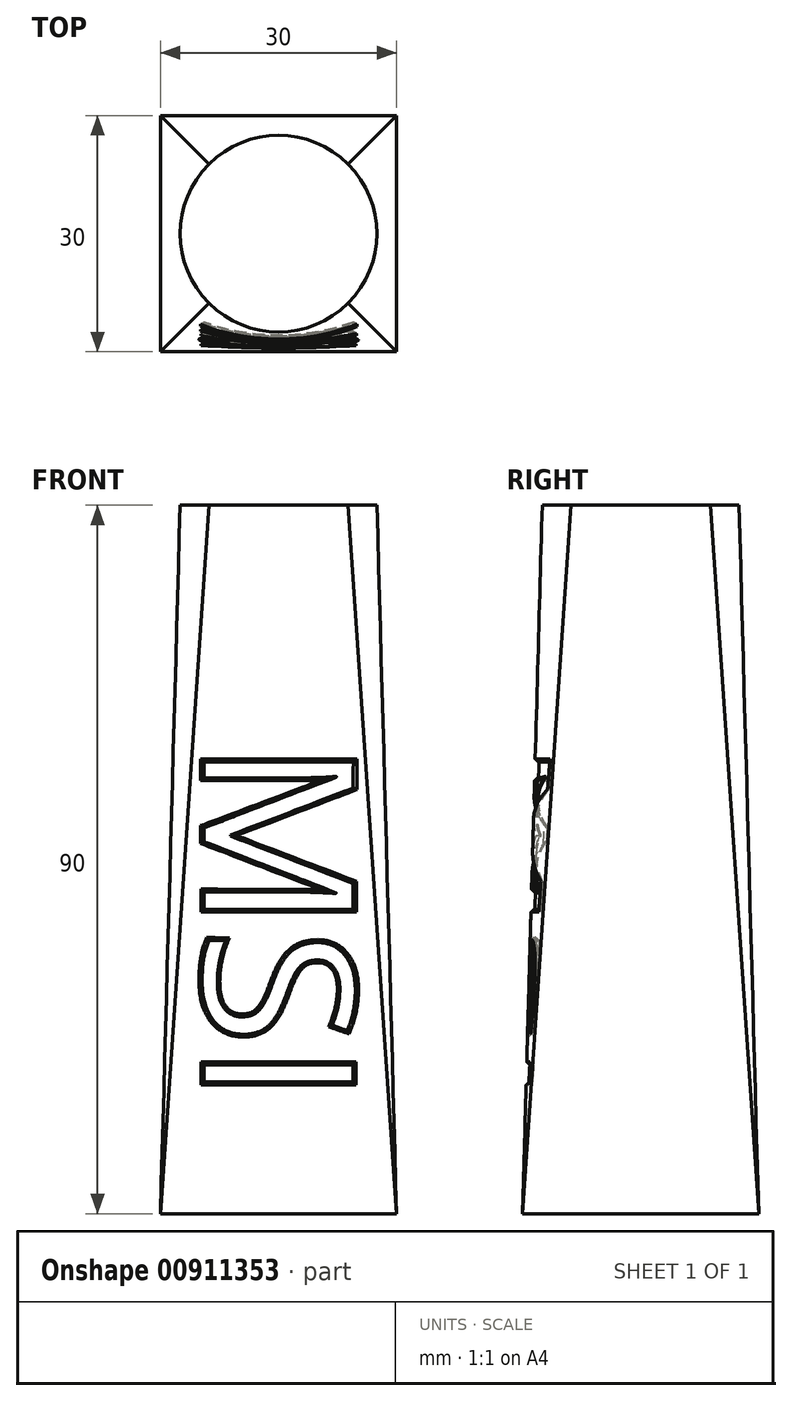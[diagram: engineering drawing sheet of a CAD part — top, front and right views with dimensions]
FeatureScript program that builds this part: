
annotation { "Feature Type Name" : "Feature", "Feature Type Description" : "" }
export const myFeature = defineFeature(function(context is Context, id is Id, definition is map)
    precondition{}
    {
        {
            var Q0;
            Q0=qCreatedBy(makeId("Top.planeOp"),FACE);
            var sketch = newSketch(context, id + "F0", { "sketchPlane" : qUnion([Q0])});
            skLineSegment(sketch, "E0.bottom", {"start": v(15, -15) * mm, "end": v(-15, -15) * mm});
            skLineSegment(sketch, "E0.top", {"start": v(15, 15) * mm, "end": v(-15, 15) * mm});
            skLineSegment(sketch, "E0.left", {"start": v(15, -15) * mm, "end": v(15, 15) * mm});
            skLineSegment(sketch, "E0.right", {"start": v(-15, -15) * mm, "end": v(-15, 15) * mm});
            skPoint(sketch, "E0.middle", {"position": v(0, 0) * mm});
            skSolve(sketch);
        }
        {
            var Q0;
            Q0=qCreatedBy(makeId("Top.planeOp"),FACE);
            cPlane(context, id + "F1", {"entities" : qUnion([Q0]), "cplaneType" : CPlaneType.OFFSET, "offset" : 90 * mm, "width" : 150 * mm, "height" : 150 * mm});
        }
        {
            var Q0;
            Q0=qCreatedBy(id+"F1.planeOp",FACE);
            var sketch = newSketch(context, id + "F2", { "sketchPlane" : qUnion([Q0])});
            skCircle(sketch, "E1", {"center": v(0, 0) * mm, "radius": 12.5 * mm});
            skSolve(sketch);
        }
        {
            var Q0;
            Q0=makeQuery(id+"F2.imprint","IMPRINT",FACE,{"disambiguationData":[TD([[makeQuery(id+"F2.imprint","IMPRINT",EDGE,{"derivedFrom":sQuery(id+"F2.wireOp",EDGE,"E1")}),1.0]])]});
            var Q1;
            Q1=makeQuery(id+"F0.imprint","IMPRINT",FACE,{"disambiguationData":[TD([[makeQuery(id+"F0.imprint","IMPRINT",EDGE,{"derivedFrom":sQuery(id+"F0.wireOp",EDGE,"E0.bottom")}),-1.0]])]});
            loft(context, id + "F3", {"sheetProfilesArray" : [{ "sheetProfileEntities" : qUnion([Q0]) }, { "sheetProfileEntities" : qUnion([Q1]) }]});
        }
        {
            var Q0;
            Q0=qCreatedBy(makeId("Front.planeOp"),FACE);
            cPlane(context, id + "F4", {"entities" : qUnion([Q0]), "cplaneType" : CPlaneType.OFFSET, "offset" : 75 * mm, "width" : 150 * mm, "height" : 150 * mm});
        }
        {
            var Q0;
            Q0=qCreatedBy(id+"F4.planeOp",FACE);
            var sketch = newSketch(context, id + "F5", { "sketchPlane" : qUnion([Q0])});
            skText(sketch, "E2", { "text": "MSI", "fontName": "OpenSans-Regular.ttf"});
            const initialGuessF5  = {"E2": [-0.00944, 0.06, 0, -1, 0.01909]};
            skSetInitialGuess(sketch, initialGuessF5);
            skSolve(sketch);
        }
        {
            var Q0;
            Q0=qSketchRegion(id+"F5",true);
            var Q1;
            Q1=makeQuery(id+"F3.opLoft","SWEPT_BODY",BODY,{"disambiguationData":[OSD([makeQuery(id+"F0.imprint","IMPRINT",FACE,{"disambiguationData":[TD([[makeQuery(id+"F0.imprint","IMPRINT",EDGE,{"derivedFrom":sQuery(id+"F0.wireOp",EDGE,"E0.bottom")}),-1.0]])]}),makeQuery(id+"F2.imprint","IMPRINT",FACE,{"disambiguationData":[TD([[makeQuery(id+"F2.imprint","IMPRINT",EDGE,{"derivedFrom":sQuery(id+"F2.wireOp",EDGE,"E1")}),1.0]])]})])]});
            extrude(context, id + "F6", {"entities" : qUnion([Q0]), "operationType" : NewBodyOperationType.REMOVE, "endBound" : BoundingType.UP_TO_BODY, "oppositeDirection" : true, "depth" : 25 * mm, "endBoundEntityBody" : qUnion([Q1]), "hasOffset" : true, "offsetDistance" : .5 * mm, "offsetOppositeDirection" : true});
        }
        {
            var Q0;
            Q0=makeQuery(id+"F6.boolean.opBoolean","INTERSECT",EDGE,{"derivedFrom":[makeQuery(id+"F3.opLoft","SWEPT_FACE",FACE,{"disambiguationData":[OSD([sQuery(id+"F0.wireOp",EDGE,"E0.bottom"),sQuery(id+"F0.wireOp",EDGE,"E0.left"),sQuery(id+"F0.wireOp",EDGE,"E0.right"),sQuery(id+"F2.wireOp",EDGE,"E1")])]}),makeQuery(id+"F6.opExtrude","SWEPT_FACE",FACE,{"disambiguationData":[OSD([sQuery(id+"F5.wireOp",EDGE,"E2.sketch_text.stroke-0")])]})]});
            var Q1;
            Q1=makeQuery(id+"F6.boolean.opBoolean","INTERSECT",EDGE,{"derivedFrom":[makeQuery(id+"F3.opLoft","SWEPT_FACE",FACE,{"disambiguationData":[OSD([sQuery(id+"F0.wireOp",EDGE,"E0.bottom"),sQuery(id+"F0.wireOp",EDGE,"E0.left"),sQuery(id+"F0.wireOp",EDGE,"E0.right"),sQuery(id+"F2.wireOp",EDGE,"E1")])]}),makeQuery(id+"F6.opExtrude","SWEPT_FACE",FACE,{"disambiguationData":[OSD([sQuery(id+"F5.wireOp",EDGE,"E2.sketch_text.stroke-7")])]})]});
            var Q2;
            Q2=makeQuery(id+"F6.boolean.opBoolean","INTERSECT",EDGE,{"derivedFrom":[makeQuery(id+"F3.opLoft","SWEPT_FACE",FACE,{"disambiguationData":[OSD([sQuery(id+"F0.wireOp",EDGE,"E0.bottom"),sQuery(id+"F0.wireOp",EDGE,"E0.left"),sQuery(id+"F0.wireOp",EDGE,"E0.right"),sQuery(id+"F2.wireOp",EDGE,"E1")])]}),makeQuery(id+"F6.opExtrude","SWEPT_FACE",FACE,{"disambiguationData":[OSD([sQuery(id+"F5.wireOp",EDGE,"E2.sketch_text.stroke-9")])]})]});
            var Q3;
            Q3=makeQuery(id+"F6.boolean.opBoolean","INTERSECT",EDGE,{"derivedFrom":[makeQuery(id+"F3.opLoft","SWEPT_FACE",FACE,{"disambiguationData":[OSD([sQuery(id+"F0.wireOp",EDGE,"E0.bottom"),sQuery(id+"F0.wireOp",EDGE,"E0.left"),sQuery(id+"F0.wireOp",EDGE,"E0.right"),sQuery(id+"F2.wireOp",EDGE,"E1")])]}),makeQuery(id+"F6.opExtrude","SWEPT_FACE",FACE,{"disambiguationData":[OSD([sQuery(id+"F5.wireOp",EDGE,"E2.sketch_text.stroke-5")])]})]});
            var Q4;
            Q4=makeQuery(id+"F6.boolean.opBoolean","INTERSECT",EDGE,{"derivedFrom":[makeQuery(id+"F3.opLoft","SWEPT_FACE",FACE,{"disambiguationData":[OSD([sQuery(id+"F0.wireOp",EDGE,"E0.bottom"),sQuery(id+"F0.wireOp",EDGE,"E0.left"),sQuery(id+"F0.wireOp",EDGE,"E0.right"),sQuery(id+"F2.wireOp",EDGE,"E1")])]}),makeQuery(id+"F6.opExtrude","SWEPT_FACE",FACE,{"disambiguationData":[OSD([sQuery(id+"F5.wireOp",EDGE,"E2.sketch_text.stroke-6")])]})]});
            var Q5;
            Q5=makeQuery(id+"F6.boolean.opBoolean","INTERSECT",EDGE,{"derivedFrom":[makeQuery(id+"F3.opLoft","SWEPT_FACE",FACE,{"disambiguationData":[OSD([sQuery(id+"F0.wireOp",EDGE,"E0.bottom"),sQuery(id+"F0.wireOp",EDGE,"E0.left"),sQuery(id+"F0.wireOp",EDGE,"E0.right"),sQuery(id+"F2.wireOp",EDGE,"E1")])]}),makeQuery(id+"F6.opExtrude","SWEPT_FACE",FACE,{"disambiguationData":[OSD([sQuery(id+"F5.wireOp",EDGE,"E2.sketch_text.stroke-4")])]})]});
            var Q6;
            Q6=makeQuery(id+"F6.boolean.opBoolean","INTERSECT",EDGE,{"derivedFrom":[makeQuery(id+"F3.opLoft","SWEPT_FACE",FACE,{"disambiguationData":[OSD([sQuery(id+"F0.wireOp",EDGE,"E0.bottom"),sQuery(id+"F0.wireOp",EDGE,"E0.left"),sQuery(id+"F0.wireOp",EDGE,"E0.right"),sQuery(id+"F2.wireOp",EDGE,"E1")])]}),makeQuery(id+"F6.opExtrude","SWEPT_FACE",FACE,{"disambiguationData":[OSD([sQuery(id+"F5.wireOp",EDGE,"E2.sketch_text.stroke-3")])]})]});
            var Q7;
            Q7=makeQuery(id+"F6.boolean.opBoolean","INTERSECT",EDGE,{"derivedFrom":[makeQuery(id+"F3.opLoft","SWEPT_FACE",FACE,{"disambiguationData":[OSD([sQuery(id+"F0.wireOp",EDGE,"E0.bottom"),sQuery(id+"F0.wireOp",EDGE,"E0.left"),sQuery(id+"F0.wireOp",EDGE,"E0.right"),sQuery(id+"F2.wireOp",EDGE,"E1")])]}),makeQuery(id+"F6.opExtrude","SWEPT_FACE",FACE,{"disambiguationData":[OSD([sQuery(id+"F5.wireOp",EDGE,"E2.sketch_text.stroke-2")])]})]});
            var Q8;
            Q8=makeQuery(id+"F6.boolean.opBoolean","INTERSECT",EDGE,{"derivedFrom":[makeQuery(id+"F3.opLoft","SWEPT_FACE",FACE,{"disambiguationData":[OSD([sQuery(id+"F0.wireOp",EDGE,"E0.bottom"),sQuery(id+"F0.wireOp",EDGE,"E0.left"),sQuery(id+"F0.wireOp",EDGE,"E0.right"),sQuery(id+"F2.wireOp",EDGE,"E1")])]}),makeQuery(id+"F6.opExtrude","SWEPT_FACE",FACE,{"disambiguationData":[OSD([sQuery(id+"F5.wireOp",EDGE,"E2.sketch_text.stroke-17")])]})]});
            var Q9;
            Q9=makeQuery(id+"F6.boolean.opBoolean","INTERSECT",EDGE,{"derivedFrom":[makeQuery(id+"F3.opLoft","SWEPT_FACE",FACE,{"disambiguationData":[OSD([sQuery(id+"F0.wireOp",EDGE,"E0.bottom"),sQuery(id+"F0.wireOp",EDGE,"E0.left"),sQuery(id+"F0.wireOp",EDGE,"E0.right"),sQuery(id+"F2.wireOp",EDGE,"E1")])]}),makeQuery(id+"F6.opExtrude","SWEPT_FACE",FACE,{"disambiguationData":[OSD([sQuery(id+"F5.wireOp",EDGE,"E2.sketch_text.stroke-16")])]})]});
            var Q10;
            Q10=makeQuery(id+"F6.boolean.opBoolean","INTERSECT",EDGE,{"derivedFrom":[makeQuery(id+"F3.opLoft","SWEPT_FACE",FACE,{"disambiguationData":[OSD([sQuery(id+"F0.wireOp",EDGE,"E0.bottom"),sQuery(id+"F0.wireOp",EDGE,"E0.left"),sQuery(id+"F0.wireOp",EDGE,"E0.right"),sQuery(id+"F2.wireOp",EDGE,"E1")])]}),makeQuery(id+"F6.opExtrude","SWEPT_FACE",FACE,{"disambiguationData":[OSD([sQuery(id+"F5.wireOp",EDGE,"E2.sketch_text.stroke-14")])]})]});
            var Q11;
            Q11=makeQuery(id+"F6.boolean.opBoolean","INTERSECT",EDGE,{"derivedFrom":[makeQuery(id+"F3.opLoft","SWEPT_FACE",FACE,{"disambiguationData":[OSD([sQuery(id+"F0.wireOp",EDGE,"E0.bottom"),sQuery(id+"F0.wireOp",EDGE,"E0.left"),sQuery(id+"F0.wireOp",EDGE,"E0.right"),sQuery(id+"F2.wireOp",EDGE,"E1")])]}),makeQuery(id+"F6.opExtrude","SWEPT_FACE",FACE,{"disambiguationData":[OSD([sQuery(id+"F5.wireOp",EDGE,"E2.sketch_text.stroke-13")])]})]});
            var Q12;
            Q12=makeQuery(id+"F6.boolean.opBoolean","INTERSECT",EDGE,{"derivedFrom":[makeQuery(id+"F3.opLoft","SWEPT_FACE",FACE,{"disambiguationData":[OSD([sQuery(id+"F0.wireOp",EDGE,"E0.bottom"),sQuery(id+"F0.wireOp",EDGE,"E0.left"),sQuery(id+"F0.wireOp",EDGE,"E0.right"),sQuery(id+"F2.wireOp",EDGE,"E1")])]}),makeQuery(id+"F6.opExtrude","SWEPT_FACE",FACE,{"disambiguationData":[OSD([sQuery(id+"F5.wireOp",EDGE,"E2.sketch_text.stroke-12")])]})]});
            var Q13;
            Q13=makeQuery(id+"F6.boolean.opBoolean","INTERSECT",EDGE,{"derivedFrom":[makeQuery(id+"F3.opLoft","SWEPT_FACE",FACE,{"disambiguationData":[OSD([sQuery(id+"F0.wireOp",EDGE,"E0.bottom"),sQuery(id+"F0.wireOp",EDGE,"E0.left"),sQuery(id+"F0.wireOp",EDGE,"E0.right"),sQuery(id+"F2.wireOp",EDGE,"E1")])]}),makeQuery(id+"F6.opExtrude","SWEPT_FACE",FACE,{"disambiguationData":[OSD([sQuery(id+"F5.wireOp",EDGE,"E2.sketch_text.stroke-11")])]})]});
            var Q14;
            Q14=makeQuery(id+"F6.boolean.opBoolean","INTERSECT",EDGE,{"derivedFrom":[makeQuery(id+"F3.opLoft","SWEPT_FACE",FACE,{"disambiguationData":[OSD([sQuery(id+"F0.wireOp",EDGE,"E0.bottom"),sQuery(id+"F0.wireOp",EDGE,"E0.left"),sQuery(id+"F0.wireOp",EDGE,"E0.right"),sQuery(id+"F2.wireOp",EDGE,"E1")])]}),makeQuery(id+"F6.opExtrude","SWEPT_FACE",FACE,{"disambiguationData":[OSD([sQuery(id+"F5.wireOp",EDGE,"E2.sketch_text.stroke-10")])]})]});
            var Q15;
            Q15=makeQuery(id+"F6.boolean.opBoolean","INTERSECT",EDGE,{"derivedFrom":[makeQuery(id+"F3.opLoft","SWEPT_FACE",FACE,{"disambiguationData":[OSD([sQuery(id+"F0.wireOp",EDGE,"E0.bottom"),sQuery(id+"F0.wireOp",EDGE,"E0.left"),sQuery(id+"F0.wireOp",EDGE,"E0.right"),sQuery(id+"F2.wireOp",EDGE,"E1")])]}),makeQuery(id+"F6.opExtrude","SWEPT_FACE",FACE,{"disambiguationData":[OSD([sQuery(id+"F5.wireOp",EDGE,"E2.sketch_text.stroke-32")])]})]});
            var Q16;
            Q16=makeQuery(id+"F6.boolean.opBoolean","INTERSECT",EDGE,{"derivedFrom":[makeQuery(id+"F3.opLoft","SWEPT_FACE",FACE,{"disambiguationData":[OSD([sQuery(id+"F0.wireOp",EDGE,"E0.bottom"),sQuery(id+"F0.wireOp",EDGE,"E0.left"),sQuery(id+"F0.wireOp",EDGE,"E0.right"),sQuery(id+"F2.wireOp",EDGE,"E1")])]}),makeQuery(id+"F6.opExtrude","SWEPT_FACE",FACE,{"disambiguationData":[OSD([sQuery(id+"F5.wireOp",EDGE,"E2.sketch_text.stroke-31")])]})]});
            var Q17;
            Q17=makeQuery(id+"F6.boolean.opBoolean","INTERSECT",EDGE,{"derivedFrom":[makeQuery(id+"F3.opLoft","SWEPT_FACE",FACE,{"disambiguationData":[OSD([sQuery(id+"F0.wireOp",EDGE,"E0.bottom"),sQuery(id+"F0.wireOp",EDGE,"E0.left"),sQuery(id+"F0.wireOp",EDGE,"E0.right"),sQuery(id+"F2.wireOp",EDGE,"E1")])]}),makeQuery(id+"F6.opExtrude","SWEPT_FACE",FACE,{"disambiguationData":[OSD([sQuery(id+"F5.wireOp",EDGE,"E2.sketch_text.stroke-30")])]})]});
            var Q18;
            Q18=makeQuery(id+"F6.boolean.opBoolean","INTERSECT",EDGE,{"derivedFrom":[makeQuery(id+"F3.opLoft","SWEPT_FACE",FACE,{"disambiguationData":[OSD([sQuery(id+"F0.wireOp",EDGE,"E0.bottom"),sQuery(id+"F0.wireOp",EDGE,"E0.left"),sQuery(id+"F0.wireOp",EDGE,"E0.right"),sQuery(id+"F2.wireOp",EDGE,"E1")])]}),makeQuery(id+"F6.opExtrude","SWEPT_FACE",FACE,{"disambiguationData":[OSD([sQuery(id+"F5.wireOp",EDGE,"E2.sketch_text.stroke-29")])]})]});
            var Q19;
            Q19=makeQuery(id+"F6.boolean.opBoolean","INTERSECT",EDGE,{"derivedFrom":[makeQuery(id+"F3.opLoft","SWEPT_FACE",FACE,{"disambiguationData":[OSD([sQuery(id+"F0.wireOp",EDGE,"E0.bottom"),sQuery(id+"F0.wireOp",EDGE,"E0.left"),sQuery(id+"F0.wireOp",EDGE,"E0.right"),sQuery(id+"F2.wireOp",EDGE,"E1")])]}),makeQuery(id+"F6.opExtrude","SWEPT_FACE",FACE,{"disambiguationData":[OSD([sQuery(id+"F5.wireOp",EDGE,"E2.sketch_text.stroke-28")])]})]});
            var Q20;
            Q20=makeQuery(id+"F6.boolean.opBoolean","INTERSECT",EDGE,{"derivedFrom":[makeQuery(id+"F3.opLoft","SWEPT_FACE",FACE,{"disambiguationData":[OSD([sQuery(id+"F0.wireOp",EDGE,"E0.bottom"),sQuery(id+"F0.wireOp",EDGE,"E0.left"),sQuery(id+"F0.wireOp",EDGE,"E0.right"),sQuery(id+"F2.wireOp",EDGE,"E1")])]}),makeQuery(id+"F6.opExtrude","SWEPT_FACE",FACE,{"disambiguationData":[OSD([sQuery(id+"F5.wireOp",EDGE,"E2.sketch_text.stroke-27")])]})]});
            var Q21;
            Q21=makeQuery(id+"F6.boolean.opBoolean","INTERSECT",EDGE,{"derivedFrom":[makeQuery(id+"F3.opLoft","SWEPT_FACE",FACE,{"disambiguationData":[OSD([sQuery(id+"F0.wireOp",EDGE,"E0.bottom"),sQuery(id+"F0.wireOp",EDGE,"E0.left"),sQuery(id+"F0.wireOp",EDGE,"E0.right"),sQuery(id+"F2.wireOp",EDGE,"E1")])]}),makeQuery(id+"F6.opExtrude","SWEPT_FACE",FACE,{"disambiguationData":[OSD([sQuery(id+"F5.wireOp",EDGE,"E2.sketch_text.stroke-26")])]})]});
            var Q22;
            Q22=makeQuery(id+"F6.boolean.opBoolean","INTERSECT",EDGE,{"derivedFrom":[makeQuery(id+"F3.opLoft","SWEPT_FACE",FACE,{"disambiguationData":[OSD([sQuery(id+"F0.wireOp",EDGE,"E0.bottom"),sQuery(id+"F0.wireOp",EDGE,"E0.left"),sQuery(id+"F0.wireOp",EDGE,"E0.right"),sQuery(id+"F2.wireOp",EDGE,"E1")])]}),makeQuery(id+"F6.opExtrude","SWEPT_FACE",FACE,{"disambiguationData":[OSD([sQuery(id+"F5.wireOp",EDGE,"E2.sketch_text.stroke-25")])]})]});
            var Q23;
            Q23=makeQuery(id+"F6.boolean.opBoolean","INTERSECT",EDGE,{"derivedFrom":[makeQuery(id+"F3.opLoft","SWEPT_FACE",FACE,{"disambiguationData":[OSD([sQuery(id+"F0.wireOp",EDGE,"E0.bottom"),sQuery(id+"F0.wireOp",EDGE,"E0.left"),sQuery(id+"F0.wireOp",EDGE,"E0.right"),sQuery(id+"F2.wireOp",EDGE,"E1")])]}),makeQuery(id+"F6.opExtrude","SWEPT_FACE",FACE,{"disambiguationData":[OSD([sQuery(id+"F5.wireOp",EDGE,"E2.sketch_text.stroke-24")])]})]});
            var Q24;
            Q24=makeQuery(id+"F6.boolean.opBoolean","INTERSECT",EDGE,{"derivedFrom":[makeQuery(id+"F3.opLoft","SWEPT_FACE",FACE,{"disambiguationData":[OSD([sQuery(id+"F0.wireOp",EDGE,"E0.bottom"),sQuery(id+"F0.wireOp",EDGE,"E0.left"),sQuery(id+"F0.wireOp",EDGE,"E0.right"),sQuery(id+"F2.wireOp",EDGE,"E1")])]}),makeQuery(id+"F6.opExtrude","SWEPT_FACE",FACE,{"disambiguationData":[OSD([sQuery(id+"F5.wireOp",EDGE,"E2.sketch_text.stroke-23")])]})]});
            var Q25;
            Q25=makeQuery(id+"F6.boolean.opBoolean","INTERSECT",EDGE,{"derivedFrom":[makeQuery(id+"F3.opLoft","SWEPT_FACE",FACE,{"disambiguationData":[OSD([sQuery(id+"F0.wireOp",EDGE,"E0.bottom"),sQuery(id+"F0.wireOp",EDGE,"E0.left"),sQuery(id+"F0.wireOp",EDGE,"E0.right"),sQuery(id+"F2.wireOp",EDGE,"E1")])]}),makeQuery(id+"F6.opExtrude","SWEPT_FACE",FACE,{"disambiguationData":[OSD([sQuery(id+"F5.wireOp",EDGE,"E2.sketch_text.stroke-22")])]})]});
            var Q26;
            Q26=makeQuery(id+"F6.boolean.opBoolean","INTERSECT",EDGE,{"derivedFrom":[makeQuery(id+"F3.opLoft","SWEPT_FACE",FACE,{"disambiguationData":[OSD([sQuery(id+"F0.wireOp",EDGE,"E0.bottom"),sQuery(id+"F0.wireOp",EDGE,"E0.left"),sQuery(id+"F0.wireOp",EDGE,"E0.right"),sQuery(id+"F2.wireOp",EDGE,"E1")])]}),makeQuery(id+"F6.opExtrude","SWEPT_FACE",FACE,{"disambiguationData":[OSD([sQuery(id+"F5.wireOp",EDGE,"E2.sketch_text.stroke-21")])]})]});
            var Q27;
            Q27=makeQuery(id+"F6.boolean.opBoolean","INTERSECT",EDGE,{"derivedFrom":[makeQuery(id+"F3.opLoft","SWEPT_FACE",FACE,{"disambiguationData":[OSD([sQuery(id+"F0.wireOp",EDGE,"E0.bottom"),sQuery(id+"F0.wireOp",EDGE,"E0.left"),sQuery(id+"F0.wireOp",EDGE,"E0.right"),sQuery(id+"F2.wireOp",EDGE,"E1")])]}),makeQuery(id+"F6.opExtrude","SWEPT_FACE",FACE,{"disambiguationData":[OSD([sQuery(id+"F5.wireOp",EDGE,"E2.sketch_text.stroke-20")])]})]});
            var Q28;
            Q28=makeQuery(id+"F6.boolean.opBoolean","INTERSECT",EDGE,{"derivedFrom":[makeQuery(id+"F3.opLoft","SWEPT_FACE",FACE,{"disambiguationData":[OSD([sQuery(id+"F0.wireOp",EDGE,"E0.bottom"),sQuery(id+"F0.wireOp",EDGE,"E0.left"),sQuery(id+"F0.wireOp",EDGE,"E0.right"),sQuery(id+"F2.wireOp",EDGE,"E1")])]}),makeQuery(id+"F6.opExtrude","SWEPT_FACE",FACE,{"disambiguationData":[OSD([sQuery(id+"F5.wireOp",EDGE,"E2.sketch_text.stroke-19")])]})]});
            var Q29;
            Q29=makeQuery(id+"F6.boolean.opBoolean","INTERSECT",EDGE,{"derivedFrom":[makeQuery(id+"F3.opLoft","SWEPT_FACE",FACE,{"disambiguationData":[OSD([sQuery(id+"F0.wireOp",EDGE,"E0.bottom"),sQuery(id+"F0.wireOp",EDGE,"E0.left"),sQuery(id+"F0.wireOp",EDGE,"E0.right"),sQuery(id+"F2.wireOp",EDGE,"E1")])]}),makeQuery(id+"F6.opExtrude","SWEPT_FACE",FACE,{"disambiguationData":[OSD([sQuery(id+"F5.wireOp",EDGE,"E2.sketch_text.stroke-18")])]})]});
            var Q30;
            Q30=makeQuery(id+"F6.boolean.opBoolean","INTERSECT",EDGE,{"derivedFrom":[makeQuery(id+"F3.opLoft","SWEPT_FACE",FACE,{"disambiguationData":[OSD([sQuery(id+"F0.wireOp",EDGE,"E0.bottom"),sQuery(id+"F0.wireOp",EDGE,"E0.left"),sQuery(id+"F0.wireOp",EDGE,"E0.right"),sQuery(id+"F2.wireOp",EDGE,"E1")])]}),makeQuery(id+"F6.opExtrude","SWEPT_FACE",FACE,{"disambiguationData":[OSD([sQuery(id+"F5.wireOp",EDGE,"E2.sketch_text.stroke-42")])]})]});
            var Q31;
            Q31=makeQuery(id+"F6.boolean.opBoolean","INTERSECT",EDGE,{"derivedFrom":[makeQuery(id+"F3.opLoft","SWEPT_FACE",FACE,{"disambiguationData":[OSD([sQuery(id+"F0.wireOp",EDGE,"E0.bottom"),sQuery(id+"F0.wireOp",EDGE,"E0.left"),sQuery(id+"F0.wireOp",EDGE,"E0.right"),sQuery(id+"F2.wireOp",EDGE,"E1")])]}),makeQuery(id+"F6.opExtrude","SWEPT_FACE",FACE,{"disambiguationData":[OSD([sQuery(id+"F5.wireOp",EDGE,"E2.sketch_text.stroke-41")])]})]});
            var Q32;
            Q32=makeQuery(id+"F6.boolean.opBoolean","INTERSECT",EDGE,{"derivedFrom":[makeQuery(id+"F3.opLoft","SWEPT_FACE",FACE,{"disambiguationData":[OSD([sQuery(id+"F0.wireOp",EDGE,"E0.bottom"),sQuery(id+"F0.wireOp",EDGE,"E0.left"),sQuery(id+"F0.wireOp",EDGE,"E0.right"),sQuery(id+"F2.wireOp",EDGE,"E1")])]}),makeQuery(id+"F6.opExtrude","SWEPT_FACE",FACE,{"disambiguationData":[OSD([sQuery(id+"F5.wireOp",EDGE,"E2.sketch_text.stroke-40")])]})]});
            var Q33;
            Q33=makeQuery(id+"F6.boolean.opBoolean","INTERSECT",EDGE,{"derivedFrom":[makeQuery(id+"F3.opLoft","SWEPT_FACE",FACE,{"disambiguationData":[OSD([sQuery(id+"F0.wireOp",EDGE,"E0.bottom"),sQuery(id+"F0.wireOp",EDGE,"E0.left"),sQuery(id+"F0.wireOp",EDGE,"E0.right"),sQuery(id+"F2.wireOp",EDGE,"E1")])]}),makeQuery(id+"F6.opExtrude","SWEPT_FACE",FACE,{"disambiguationData":[OSD([sQuery(id+"F5.wireOp",EDGE,"E2.sketch_text.stroke-39")])]})]});
            var Q34;
            Q34=makeQuery(id+"F6.boolean.opBoolean","INTERSECT",EDGE,{"derivedFrom":[makeQuery(id+"F3.opLoft","SWEPT_FACE",FACE,{"disambiguationData":[OSD([sQuery(id+"F0.wireOp",EDGE,"E0.bottom"),sQuery(id+"F0.wireOp",EDGE,"E0.left"),sQuery(id+"F0.wireOp",EDGE,"E0.right"),sQuery(id+"F2.wireOp",EDGE,"E1")])]}),makeQuery(id+"F6.opExtrude","SWEPT_FACE",FACE,{"disambiguationData":[OSD([sQuery(id+"F5.wireOp",EDGE,"E2.sketch_text.stroke-38")])]})]});
            var Q35;
            Q35=makeQuery(id+"F6.boolean.opBoolean","INTERSECT",EDGE,{"derivedFrom":[makeQuery(id+"F3.opLoft","SWEPT_FACE",FACE,{"disambiguationData":[OSD([sQuery(id+"F0.wireOp",EDGE,"E0.bottom"),sQuery(id+"F0.wireOp",EDGE,"E0.left"),sQuery(id+"F0.wireOp",EDGE,"E0.right"),sQuery(id+"F2.wireOp",EDGE,"E1")])]}),makeQuery(id+"F6.opExtrude","SWEPT_FACE",FACE,{"disambiguationData":[OSD([sQuery(id+"F5.wireOp",EDGE,"E2.sketch_text.stroke-37")])]})]});
            var Q36;
            Q36=makeQuery(id+"F6.boolean.opBoolean","INTERSECT",EDGE,{"derivedFrom":[makeQuery(id+"F3.opLoft","SWEPT_FACE",FACE,{"disambiguationData":[OSD([sQuery(id+"F0.wireOp",EDGE,"E0.bottom"),sQuery(id+"F0.wireOp",EDGE,"E0.left"),sQuery(id+"F0.wireOp",EDGE,"E0.right"),sQuery(id+"F2.wireOp",EDGE,"E1")])]}),makeQuery(id+"F6.opExtrude","SWEPT_FACE",FACE,{"disambiguationData":[OSD([sQuery(id+"F5.wireOp",EDGE,"E2.sketch_text.stroke-36")])]})]});
            var Q37;
            Q37=makeQuery(id+"F6.boolean.opBoolean","INTERSECT",EDGE,{"derivedFrom":[makeQuery(id+"F3.opLoft","SWEPT_FACE",FACE,{"disambiguationData":[OSD([sQuery(id+"F0.wireOp",EDGE,"E0.bottom"),sQuery(id+"F0.wireOp",EDGE,"E0.left"),sQuery(id+"F0.wireOp",EDGE,"E0.right"),sQuery(id+"F2.wireOp",EDGE,"E1")])]}),makeQuery(id+"F6.opExtrude","SWEPT_FACE",FACE,{"disambiguationData":[OSD([sQuery(id+"F5.wireOp",EDGE,"E2.sketch_text.stroke-35")])]})]});
            var Q38;
            Q38=makeQuery(id+"F6.boolean.opBoolean","INTERSECT",EDGE,{"derivedFrom":[makeQuery(id+"F3.opLoft","SWEPT_FACE",FACE,{"disambiguationData":[OSD([sQuery(id+"F0.wireOp",EDGE,"E0.bottom"),sQuery(id+"F0.wireOp",EDGE,"E0.left"),sQuery(id+"F0.wireOp",EDGE,"E0.right"),sQuery(id+"F2.wireOp",EDGE,"E1")])]}),makeQuery(id+"F6.opExtrude","SWEPT_FACE",FACE,{"disambiguationData":[OSD([sQuery(id+"F5.wireOp",EDGE,"E2.sketch_text.stroke-34")])]})]});
            var Q39;
            Q39=makeQuery(id+"F6.boolean.opBoolean","INTERSECT",EDGE,{"derivedFrom":[makeQuery(id+"F3.opLoft","SWEPT_FACE",FACE,{"disambiguationData":[OSD([sQuery(id+"F0.wireOp",EDGE,"E0.bottom"),sQuery(id+"F0.wireOp",EDGE,"E0.left"),sQuery(id+"F0.wireOp",EDGE,"E0.right"),sQuery(id+"F2.wireOp",EDGE,"E1")])]}),makeQuery(id+"F6.opExtrude","SWEPT_FACE",FACE,{"disambiguationData":[OSD([sQuery(id+"F5.wireOp",EDGE,"E2.sketch_text.stroke-33")])]})]});
            var Q40;
            Q40=makeQuery(id+"F6.boolean.opBoolean","INTERSECT",EDGE,{"derivedFrom":[makeQuery(id+"F3.opLoft","SWEPT_FACE",FACE,{"disambiguationData":[OSD([sQuery(id+"F0.wireOp",EDGE,"E0.bottom"),sQuery(id+"F0.wireOp",EDGE,"E0.left"),sQuery(id+"F0.wireOp",EDGE,"E0.right"),sQuery(id+"F2.wireOp",EDGE,"E1")])]}),makeQuery(id+"F6.opExtrude","SWEPT_FACE",FACE,{"disambiguationData":[OSD([sQuery(id+"F5.wireOp",EDGE,"E2.sketch_text.stroke-43")])]})]});
            var Q41;
            Q41=makeQuery(id+"F6.boolean.opBoolean","INTERSECT",EDGE,{"derivedFrom":[makeQuery(id+"F3.opLoft","SWEPT_FACE",FACE,{"disambiguationData":[OSD([sQuery(id+"F0.wireOp",EDGE,"E0.bottom"),sQuery(id+"F0.wireOp",EDGE,"E0.left"),sQuery(id+"F0.wireOp",EDGE,"E0.right"),sQuery(id+"F2.wireOp",EDGE,"E1")])]}),makeQuery(id+"F6.opExtrude","SWEPT_FACE",FACE,{"disambiguationData":[OSD([sQuery(id+"F5.wireOp",EDGE,"E2.sketch_text.stroke-44")])]})]});
            var Q42;
            Q42=makeQuery(id+"F6.boolean.opBoolean","INTERSECT",EDGE,{"derivedFrom":[makeQuery(id+"F3.opLoft","SWEPT_FACE",FACE,{"disambiguationData":[OSD([sQuery(id+"F0.wireOp",EDGE,"E0.bottom"),sQuery(id+"F0.wireOp",EDGE,"E0.left"),sQuery(id+"F0.wireOp",EDGE,"E0.right"),sQuery(id+"F2.wireOp",EDGE,"E1")])]}),makeQuery(id+"F6.opExtrude","SWEPT_FACE",FACE,{"disambiguationData":[OSD([sQuery(id+"F5.wireOp",EDGE,"E2.sketch_text.stroke-45")])]})]});
            var Q43;
            Q43=makeQuery(id+"F6.boolean.opBoolean","INTERSECT",EDGE,{"derivedFrom":[makeQuery(id+"F3.opLoft","SWEPT_FACE",FACE,{"disambiguationData":[OSD([sQuery(id+"F0.wireOp",EDGE,"E0.bottom"),sQuery(id+"F0.wireOp",EDGE,"E0.left"),sQuery(id+"F0.wireOp",EDGE,"E0.right"),sQuery(id+"F2.wireOp",EDGE,"E1")])]}),makeQuery(id+"F6.opExtrude","SWEPT_FACE",FACE,{"disambiguationData":[OSD([sQuery(id+"F5.wireOp",EDGE,"E2.sketch_text.stroke-46")])]})]});
            chamfer(context, id + "F7", {"entities" : qUnion([Q0, Q1, Q2, Q3, Q4, Q5, Q6, Q7, Q8, Q9, Q10, Q11, Q12, Q13, Q14, Q15, Q16, Q17, Q18, Q19, Q20, Q21, Q22, Q23, Q24, Q25, Q26, Q27, Q28, Q29, Q30, Q31, Q32, Q33, Q34, Q35, Q36, Q37, Q38, Q39, Q40, Q41, Q42, Q43]), "width" : .35 * mm, "tangentPropagation" : true});
        }
    });
